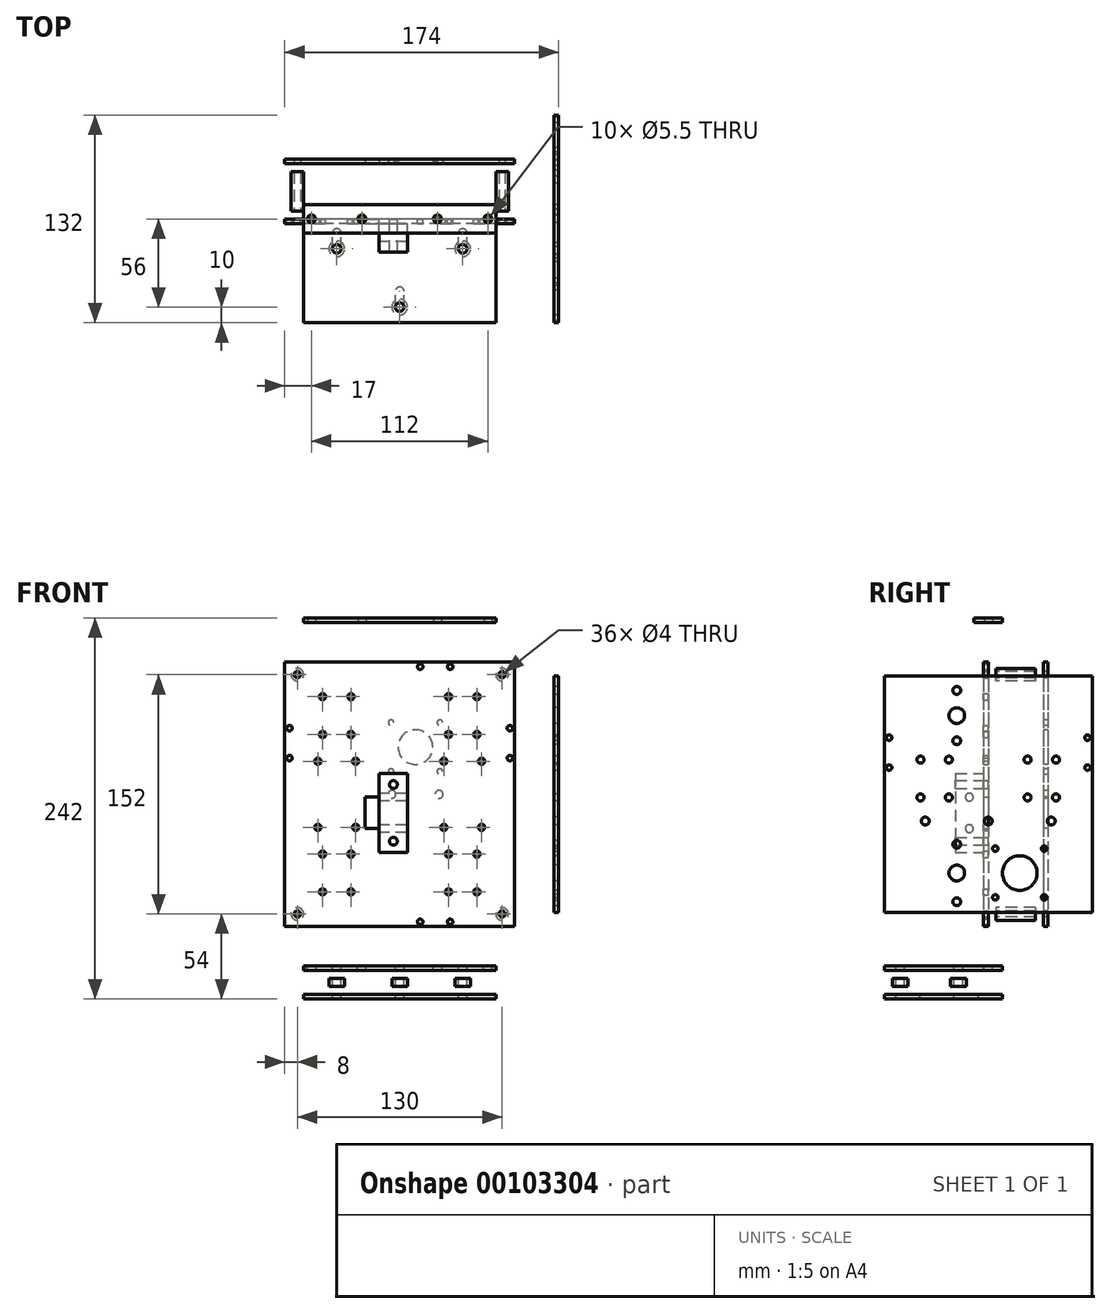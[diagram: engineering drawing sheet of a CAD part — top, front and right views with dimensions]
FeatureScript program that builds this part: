
annotation { "Feature Type Name" : "Feature", "Feature Type Description" : "" }
export const myFeature = defineFeature(function(context is Context, id is Id, definition is map)
    precondition{}
    {
        {
            assignVariable(context, id + "F0", {"name" : "Thickness", "anyValue" : 3});
        }
        {
            var Q0;
            Q0=qCreatedBy(makeId("Front.planeOp"),FACE);
            var sketch = newSketch(context, id + "F1", { "sketchPlane" : qUnion([Q0])});
            skLineSegment(sketch, "E0.bottom", {"start": v(73, 84) * mm, "end": v(-73, 84) * mm});
            skLineSegment(sketch, "E0.top", {"start": v(73, -84) * mm, "end": v(-73, -84) * mm});
            skLineSegment(sketch, "E0.left", {"start": v(73, 84) * mm, "end": v(73, -84) * mm});
            skLineSegment(sketch, "E0.right", {"start": v(-73, 84) * mm, "end": v(-73, -84) * mm});
            skPoint(sketch, "E0.middle", {"position": v(0, 0) * mm});
            skLineSegment(sketch, "E1", {"start": v(-49, -83.08) * mm, "end": v(-49, 79.73) * mm, "construction": true});
            skLineSegment(sketch, "E2", {"start": v(-31, -83.97) * mm, "end": v(-31, 79.73) * mm, "construction": true});
            skLineSegment(sketch, "E3", {"start": v(-55.64, 38) * mm, "end": v(56.55, 38) * mm, "construction": true});
            skLineSegment(sketch, "E4", {"start": v(-58.53, 62) * mm, "end": v(58.53, 62) * mm, "construction": true});
            skCircle(sketch, "E5", {"center": v(-49, 38) * mm, "radius": 2 * mm});
            skCircle(sketch, "E6", {"center": v(-49, 62) * mm, "radius": 2 * mm});
            skCircle(sketch, "E7", {"center": v(-31, 38) * mm, "radius": 2 * mm});
            skCircle(sketch, "E8", {"center": v(-31, 62) * mm, "radius": 2 * mm});
            skLineSegment(sketch, "E9", {"start": v(-72.74, 50) * mm, "end": v(58.97, 50) * mm, "construction": true});
            skLineSegment(sketch, "E10", {"start": v(-40, 79.29) * mm, "end": v(-40, -83.3) * mm, "construction": true});
            skLineSegment(sketch, "E11", {"start": v(-69.64, -50) * mm, "end": v(60.08, -50) * mm, "construction": true});
            skLineSegment(sketch, "E12", {"start": v(-58.61, -38) * mm, "end": v(58.75, -38) * mm, "construction": true});
            skLineSegment(sketch, "E13", {"start": v(-57.29, -62) * mm, "end": v(60.52, -62) * mm, "construction": true});
            skLineSegment(sketch, "E14", {"start": v(40, 79.29) * mm, "end": v(40, -84.85) * mm, "construction": true});
            skLineSegment(sketch, "E15", {"start": v(49, 79.07) * mm, "end": v(49, -84.4) * mm, "construction": true});
            skLineSegment(sketch, "E16", {"start": v(31, 79.29) * mm, "end": v(31, -83.74) * mm, "construction": true});
            skCircle(sketch, "E17", {"center": v(-49, -38) * mm, "radius": 2 * mm});
            skCircle(sketch, "E18", {"center": v(-31, -38) * mm, "radius": 2 * mm});
            skCircle(sketch, "E19", {"center": v(-49, -62) * mm, "radius": 2 * mm});
            skCircle(sketch, "E20", {"center": v(-31, -62) * mm, "radius": 2 * mm});
            skCircle(sketch, "E21", {"center": v(31, 62) * mm, "radius": 2 * mm});
            skCircle(sketch, "E22", {"center": v(49, 62) * mm, "radius": 2 * mm});
            skCircle(sketch, "E23", {"center": v(31, 38) * mm, "radius": 2 * mm});
            skCircle(sketch, "E24", {"center": v(49, 38) * mm, "radius": 2 * mm});
            skCircle(sketch, "E25", {"center": v(31, -38) * mm, "radius": 2 * mm});
            skCircle(sketch, "E26", {"center": v(49, -38) * mm, "radius": 2 * mm});
            skCircle(sketch, "E27", {"center": v(31, -62) * mm, "radius": 2 * mm});
            skCircle(sketch, "E28", {"center": v(49, -62) * mm, "radius": 2 * mm});
            skLineSegment(sketch, "E29", {"start": v(-70, 88.6) * mm, "end": v(-70, -88.82) * mm, "construction": true});
            skLineSegment(sketch, "E30", {"start": v(70, 90.06) * mm, "end": v(70, -91.23) * mm, "construction": true});
            skLineSegment(sketch, "E31", {"start": v(-72.75, 23) * mm, "end": v(68.8, 23) * mm, "construction": true});
            skCircle(sketch, "E32", {"center": v(-70, 23) * mm, "radius": 1.75 * mm});
            skCircle(sketch, "E33", {"center": v(70, 23) * mm, "radius": 1.75 * mm});
            skCircle(sketch, "E34", {"center": v(70, 42) * mm, "radius": 1.75 * mm});
            skCircle(sketch, "E35", {"center": v(-70, 42) * mm, "radius": 1.75 * mm});
            skLineSegment(sketch, "E36", {"start": v(-90.6, 21) * mm, "end": v(91.23, 21) * mm, "construction": true});
            skLineSegment(sketch, "E37", {"start": v(-89.18, -21) * mm, "end": v(89.82, -21) * mm, "construction": true});
            skLineSegment(sketch, "E38", {"start": v(28, 79.48) * mm, "end": v(28, -94.8) * mm, "construction": true});
            skLineSegment(sketch, "E39", {"start": v(52, 79.96) * mm, "end": v(52, -92.22) * mm, "construction": true});
            skLineSegment(sketch, "E40", {"start": v(-52, 80.9) * mm, "end": v(-52, -84.92) * mm, "construction": true});
            skLineSegment(sketch, "E41", {"start": v(-28, 79.72) * mm, "end": v(-28, -83.5) * mm, "construction": true});
            skCircle(sketch, "E42", {"center": v(-52, -21) * mm, "radius": 2 * mm});
            skCircle(sketch, "E43", {"center": v(-28, -21) * mm, "radius": 2 * mm});
            skCircle(sketch, "E44", {"center": v(-52, 21) * mm, "radius": 2 * mm});
            skCircle(sketch, "E45", {"center": v(-28, 21) * mm, "radius": 2 * mm});
            skCircle(sketch, "E46", {"center": v(28, 21) * mm, "radius": 2 * mm});
            skCircle(sketch, "E47", {"center": v(52, 21) * mm, "radius": 2 * mm});
            skCircle(sketch, "E48", {"center": v(52, -21) * mm, "radius": 2 * mm});
            skCircle(sketch, "E49", {"center": v(28, -21) * mm, "radius": 2 * mm});
            skLineSegment(sketch, "E50", {"start": v(-83.47, 81) * mm, "end": v(76.81, 81) * mm, "construction": true});
            skLineSegment(sketch, "E51", {"start": v(13, 80.28) * mm, "end": v(13, -83.41) * mm, "construction": true});
            skLineSegment(sketch, "E52", {"start": v(32, 79.81) * mm, "end": v(32, -83.41) * mm, "construction": true});
            skLineSegment(sketch, "E53", {"start": v(-76.56, -81) * mm, "end": v(71.61, -81) * mm, "construction": true});
            skCircle(sketch, "E54", {"center": v(13, -81) * mm, "radius": 1.75 * mm});
            skCircle(sketch, "E55", {"center": v(32, -81) * mm, "radius": 1.75 * mm});
            skCircle(sketch, "E56", {"center": v(13, 81) * mm, "radius": 1.75 * mm});
            skCircle(sketch, "E57", {"center": v(32, 81) * mm, "radius": 1.75 * mm});
            skCircle(sketch, "E58", {"center": v(-65, 76) * mm, "radius": 2 * mm});
            skCircle(sketch, "E59", {"center": v(65, 76) * mm, "radius": 2 * mm});
            skCircle(sketch, "E60", {"center": v(-65, -76) * mm, "radius": 2 * mm});
            skCircle(sketch, "E61", {"center": v(65, -76) * mm, "radius": 2 * mm});
            skLineSegment(sketch, "E62", {"start": v(-65, 88.6) * mm, "end": v(-65, -88.82) * mm, "construction": true});
            skLineSegment(sketch, "E63", {"start": v(65, 90.06) * mm, "end": v(65, -88.82) * mm, "construction": true});
            skLineSegment(sketch, "E64", {"start": v(-83.47, 76) * mm, "end": v(71.61, 76) * mm, "construction": true});
            skLineSegment(sketch, "E65", {"start": v(-76.56, -76) * mm, "end": v(71.61, -76) * mm, "construction": true});
            skLineSegment(sketch, "E66", {"start": v(-23, 79.72) * mm, "end": v(-23, -83.5) * mm, "construction": true});
            skLineSegment(sketch, "E67", {"start": v(-57, 81) * mm, "end": v(-57, -84.92) * mm, "construction": true});
            skLineSegment(sketch, "E68.bottom", {"start": v(-22, -1.8) * mm, "end": v(-13, -1.8) * mm});
            skLineSegment(sketch, "E68.top", {"start": v(-22, -21.8) * mm, "end": v(-13, -21.8) * mm});
            skLineSegment(sketch, "E68.left", {"start": v(-22, -1.8) * mm, "end": v(-22, -21.8) * mm});
            skLineSegment(sketch, "E68.right", {"start": v(-13, -1.8) * mm, "end": v(-13, -21.8) * mm});
            skLineSegment(sketch, "E69.bottom", {"start": v(-13, 13.2) * mm, "end": v(5, 13.2) * mm});
            skLineSegment(sketch, "E69.top", {"start": v(-13, -36.8) * mm, "end": v(5, -36.8) * mm});
            skLineSegment(sketch, "E69.left", {"start": v(-13, 13.2) * mm, "end": v(-13, -36.8) * mm});
            skLineSegment(sketch, "E69.right", {"start": v(5, 13.2) * mm, "end": v(5, -36.8) * mm});
            skLineSegment(sketch, "E70", {"start": v(-4, 17.89) * mm, "end": v(-4, -41.5) * mm, "construction": true});
            skCircle(sketch, "E71", {"center": v(-4, 6.2) * mm, "radius": 2.5 * mm});
            skCircle(sketch, "E72", {"center": v(-4, -29.8) * mm, "radius": 2.5 * mm});
            skLineSegment(sketch, "E73", {"start": v(-25.34, -11.8) * mm, "end": v(18.01, -11.8) * mm, "construction": true});
            skPoint(sketch, "E74", {"position": v(-4, 13.2) * mm});
            skPoint(sketch, "E75", {"position": v(-4, -11.8) * mm});
            skSolve(sketch);
        }
        {
            var Q0;
            Q0=makeQuery(id+"F1.imprint","IMPRINT",FACE,{"disambiguationData":[TD([[makeQuery(id+"F1.imprint","IMPRINT",EDGE,{"derivedFrom":sQuery(id+"F1.wireOp",EDGE,"E0.bottom")}),1.0]])]});
            var Q1;
            Q1=makeQuery(id+"F1.imprint","IMPRINT",FACE,{"disambiguationData":[TD([[makeQuery(id+"F1.imprint","IMPRINT",EDGE,{"derivedFrom":sQuery(id+"F1.wireOp",EDGE,"E69.bottom")}),-1.0]])]});
            extrude(context, id + "F2", {"entities" : qUnion([Q0, Q1]), "depth" : (getVariable(context, 'Thickness')) * mm});
        }
        {
            var Q0;
            Q0=makeQuery(id+"F1.imprint","IMPRINT",FACE,{"disambiguationData":[TD([[makeQuery(id+"F1.imprint","IMPRINT",EDGE,{"derivedFrom":sQuery(id+"F1.wireOp",EDGE,"E69.bottom")}),-1.0]])]});
            extrude(context, id + "F3", {"entities" : qUnion([Q0]), "depth" : 21 * mm, "hasSecondDirection" : true, "secondDirectionOppositeDirection" : false, "secondDirectionDepth" : 3 * mm});
        }
        {
            var Q0;
            Q0=makeQuery(id+"F3.opExtrude","SWEPT_FACE",FACE,{"disambiguationData":[OSD([sQuery(id+"F1.wireOp",EDGE,"E69.left")])]});
            var sketch = newSketch(context, id + "F4", { "sketchPlane" : qUnion([Q0])});
            skLineSegment(sketch, "E76", {"start": v(12, -1.15) * mm, "end": v(12, -40.85) * mm, "construction": true});
            skCircle(sketch, "E77", {"center": v(12, -1.8) * mm, "radius": 2.5 * mm});
            skCircle(sketch, "E78", {"center": v(12, -21.8) * mm, "radius": 2.5 * mm});
            skLineSegment(sketch, "E79", {"start": v(-1.92, -11.8) * mm, "end": v(22.84, -11.8) * mm, "construction": true});
            skCircle(sketch, "E80", {"center": v(12, -1.8) * mm, "radius": 9 * mm, "construction": true});
            skCircle(sketch, "E81", {"center": v(12, -21.8) * mm, "radius": 9 * mm, "construction": true});
            skSolve(sketch);
        }
        {
            var Q0;
            Q0=makeQuery(id+"F4.imprint","IMPRINT",FACE,{"disambiguationData":[TD([[makeQuery(id+"F4.imprint","IMPRINT",EDGE,{"derivedFrom":sQuery(id+"F4.wireOp",EDGE,"E77")}),1.0]])]});
            var Q1;
            Q1=makeQuery(id+"F4.imprint","IMPRINT",FACE,{"disambiguationData":[TD([[makeQuery(id+"F4.imprint","IMPRINT",EDGE,{"derivedFrom":sQuery(id+"F4.wireOp",EDGE,"E78")}),1.0]])]});
            extrude(context, id + "F5", {"entities" : qUnion([Q0, Q1]), "operationType" : NewBodyOperationType.REMOVE, "endBound" : BoundingType.THROUGH_ALL, "oppositeDirection" : true, "depth" : 25 * mm});
        }
        {
            var Q0;
            Q0=makeQuery(id+"F2.opExtrude","CAP_FACE",FACE,{"disambiguationData":[OSD([sQuery(id+"F1.wireOp",EDGE,"E0.bottom"),sQuery(id+"F1.wireOp",EDGE,"E0.top"),sQuery(id+"F1.wireOp",EDGE,"E0.left"),sQuery(id+"F1.wireOp",EDGE,"E0.right"),sQuery(id+"F1.wireOp",EDGE,"E5"),sQuery(id+"F1.wireOp",EDGE,"E6"),sQuery(id+"F1.wireOp",EDGE,"E7"),sQuery(id+"F1.wireOp",EDGE,"E8"),sQuery(id+"F1.wireOp",EDGE,"E17"),sQuery(id+"F1.wireOp",EDGE,"E18"),sQuery(id+"F1.wireOp",EDGE,"E19"),sQuery(id+"F1.wireOp",EDGE,"E20"),sQuery(id+"F1.wireOp",EDGE,"E21"),sQuery(id+"F1.wireOp",EDGE,"E22"),sQuery(id+"F1.wireOp",EDGE,"E23"),sQuery(id+"F1.wireOp",EDGE,"E24"),sQuery(id+"F1.wireOp",EDGE,"E25"),sQuery(id+"F1.wireOp",EDGE,"E26"),sQuery(id+"F1.wireOp",EDGE,"E27"),sQuery(id+"F1.wireOp",EDGE,"E28"),sQuery(id+"F1.wireOp",EDGE,"E32"),sQuery(id+"F1.wireOp",EDGE,"E33"),sQuery(id+"F1.wireOp",EDGE,"E34"),sQuery(id+"F1.wireOp",EDGE,"E35"),sQuery(id+"F1.wireOp",EDGE,"E42"),sQuery(id+"F1.wireOp",EDGE,"E43"),sQuery(id+"F1.wireOp",EDGE,"E44"),sQuery(id+"F1.wireOp",EDGE,"E45"),sQuery(id+"F1.wireOp",EDGE,"E46"),sQuery(id+"F1.wireOp",EDGE,"E47"),sQuery(id+"F1.wireOp",EDGE,"E48"),sQuery(id+"F1.wireOp",EDGE,"E49"),sQuery(id+"F1.wireOp",EDGE,"E54"),sQuery(id+"F1.wireOp",EDGE,"E55"),sQuery(id+"F1.wireOp",EDGE,"E56"),sQuery(id+"F1.wireOp",EDGE,"E57"),sQuery(id+"F1.wireOp",EDGE,"E58"),sQuery(id+"F1.wireOp",EDGE,"E59"),sQuery(id+"F1.wireOp",EDGE,"E60"),sQuery(id+"F1.wireOp",EDGE,"E61")])],"isStart":true});
            cPlane(context, id + "F6", {"entities" : qUnion([Q0]), "cplaneType" : CPlaneType.OFFSET, "offset" : 5 * mm, "width" : 150 * mm, "height" : 150 * mm});
        }
        {
            var Q0;
            Q0=qCreatedBy(id+"F6.planeOp",FACE);
            var sketch = newSketch(context, id + "F7", { "sketchPlane" : qUnion([Q0])});
            skCircle(sketch, "E82.0", {"center": v(65, 76) * mm, "radius": 2 * mm});
            skCircle(sketch, "E82.1", {"center": v(65, -76) * mm, "radius": 2 * mm});
            skCircle(sketch, "E82.2", {"center": v(-65, -76) * mm, "radius": 2 * mm});
            skCircle(sketch, "E82.3", {"center": v(-65, 76) * mm, "radius": 2 * mm});
            skCircle(sketch, "E83", {"center": v(65, 76) * mm, "radius": 4 * mm});
            skCircle(sketch, "E84", {"center": v(65, -76) * mm, "radius": 4 * mm});
            skCircle(sketch, "E85", {"center": v(-65, -76) * mm, "radius": 4 * mm});
            skCircle(sketch, "E86", {"center": v(-65, 76) * mm, "radius": 4 * mm});
            skSolve(sketch);
        }
        {
            var Q0;
            Q0=makeQuery(id+"F7.imprint","IMPRINT",FACE,{"disambiguationData":[TD([[makeQuery(id+"F7.imprint","IMPRINT",EDGE,{"derivedFrom":sQuery(id+"F7.wireOp",EDGE,"E82.0")}),-1.0]])]});
            var Q1;
            Q1=makeQuery(id+"F7.imprint","IMPRINT",FACE,{"disambiguationData":[TD([[makeQuery(id+"F7.imprint","IMPRINT",EDGE,{"derivedFrom":sQuery(id+"F7.wireOp",EDGE,"E82.1")}),-1.0]])]});
            var Q2;
            Q2=makeQuery(id+"F7.imprint","IMPRINT",FACE,{"disambiguationData":[TD([[makeQuery(id+"F7.imprint","IMPRINT",EDGE,{"derivedFrom":sQuery(id+"F7.wireOp",EDGE,"E82.2")}),-1.0]])]});
            var Q3;
            Q3=makeQuery(id+"F7.imprint","IMPRINT",FACE,{"disambiguationData":[TD([[makeQuery(id+"F7.imprint","IMPRINT",EDGE,{"derivedFrom":sQuery(id+"F7.wireOp",EDGE,"E82.3")}),-1.0]])]});
            extrude(context, id + "F8", {"entities" : qUnion([Q0, Q1, Q2, Q3]), "depth" : 25 * mm});
        }
        {
            var Q0;
            Q0=makeQuery(id+"F2.opExtrude","CAP_FACE",FACE,{"disambiguationData":[OSD([sQuery(id+"F1.wireOp",EDGE,"E0.bottom"),sQuery(id+"F1.wireOp",EDGE,"E0.top"),sQuery(id+"F1.wireOp",EDGE,"E0.left"),sQuery(id+"F1.wireOp",EDGE,"E0.right"),sQuery(id+"F1.wireOp",EDGE,"E5"),sQuery(id+"F1.wireOp",EDGE,"E6"),sQuery(id+"F1.wireOp",EDGE,"E7"),sQuery(id+"F1.wireOp",EDGE,"E8"),sQuery(id+"F1.wireOp",EDGE,"E17"),sQuery(id+"F1.wireOp",EDGE,"E18"),sQuery(id+"F1.wireOp",EDGE,"E19"),sQuery(id+"F1.wireOp",EDGE,"E20"),sQuery(id+"F1.wireOp",EDGE,"E21"),sQuery(id+"F1.wireOp",EDGE,"E22"),sQuery(id+"F1.wireOp",EDGE,"E23"),sQuery(id+"F1.wireOp",EDGE,"E24"),sQuery(id+"F1.wireOp",EDGE,"E25"),sQuery(id+"F1.wireOp",EDGE,"E26"),sQuery(id+"F1.wireOp",EDGE,"E27"),sQuery(id+"F1.wireOp",EDGE,"E28"),sQuery(id+"F1.wireOp",EDGE,"E32"),sQuery(id+"F1.wireOp",EDGE,"E33"),sQuery(id+"F1.wireOp",EDGE,"E34"),sQuery(id+"F1.wireOp",EDGE,"E35"),sQuery(id+"F1.wireOp",EDGE,"E42"),sQuery(id+"F1.wireOp",EDGE,"E43"),sQuery(id+"F1.wireOp",EDGE,"E44"),sQuery(id+"F1.wireOp",EDGE,"E45"),sQuery(id+"F1.wireOp",EDGE,"E46"),sQuery(id+"F1.wireOp",EDGE,"E47"),sQuery(id+"F1.wireOp",EDGE,"E48"),sQuery(id+"F1.wireOp",EDGE,"E49"),sQuery(id+"F1.wireOp",EDGE,"E54"),sQuery(id+"F1.wireOp",EDGE,"E55"),sQuery(id+"F1.wireOp",EDGE,"E56"),sQuery(id+"F1.wireOp",EDGE,"E57"),sQuery(id+"F1.wireOp",EDGE,"E58"),sQuery(id+"F1.wireOp",EDGE,"E59"),sQuery(id+"F1.wireOp",EDGE,"E60"),sQuery(id+"F1.wireOp",EDGE,"E61")])],"isStart":true});
            cPlane(context, id + "F9", {"entities" : qUnion([Q0]), "cplaneType" : CPlaneType.OFFSET, "offset" : 35 * mm, "width" : 150 * mm, "height" : 150 * mm});
        }
        {
            var Q0;
            Q0=qCreatedBy(id+"F9.planeOp",FACE);
            var sketch = newSketch(context, id + "F10", { "sketchPlane" : qUnion([Q0])});
            skLineSegment(sketch, "E87.0", {"start": v(-73, 84) * mm, "end": v(73, 84) * mm});
            skLineSegment(sketch, "E87.1", {"start": v(-73, 84) * mm, "end": v(-73, -84) * mm});
            skLineSegment(sketch, "E87.2", {"start": v(73, 84) * mm, "end": v(73, -84) * mm});
            skLineSegment(sketch, "E87.3", {"start": v(-73, -84) * mm, "end": v(73, -84) * mm});
            skLineSegment(sketch, "E87.4", {"start": v(22, -1.8) * mm, "end": v(22, -21.8) * mm});
            skLineSegment(sketch, "E87.5", {"start": v(13, -1.8) * mm, "end": v(13, -21.8) * mm});
            skLineSegment(sketch, "E87.6", {"start": v(22, -1.8) * mm, "end": v(13, -1.8) * mm});
            skLineSegment(sketch, "E87.7", {"start": v(22, -21.8) * mm, "end": v(13, -21.8) * mm});
            skLineSegment(sketch, "E88.bottom", {"start": v(-31, 51) * mm, "end": v(11, 51) * mm, "construction": true});
            skLineSegment(sketch, "E88.top", {"start": v(-31, 9) * mm, "end": v(11, 9) * mm, "construction": true});
            skLineSegment(sketch, "E88.left", {"start": v(-31, 51) * mm, "end": v(-31, 9) * mm, "construction": true});
            skLineSegment(sketch, "E88.right", {"start": v(11, 51) * mm, "end": v(11, 9) * mm, "construction": true});
            skLineSegment(sketch, "E89", {"start": v(-10, 94.34) * mm, "end": v(-10, -34.34) * mm, "construction": true});
            skLineSegment(sketch, "E90", {"start": v(-37.71, 30) * mm, "end": v(17.71, 30) * mm});
            skLineSegment(sketch, "E91.bottom", {"start": v(-25.5, 45.5) * mm, "end": v(5.5, 45.5) * mm, "construction": true});
            skLineSegment(sketch, "E91.top", {"start": v(-25.5, 14.5) * mm, "end": v(5.5, 14.5) * mm, "construction": true});
            skLineSegment(sketch, "E91.left", {"start": v(-25.5, 45.5) * mm, "end": v(-25.5, 14.5) * mm, "construction": true});
            skLineSegment(sketch, "E91.right", {"start": v(5.5, 45.5) * mm, "end": v(5.5, 14.5) * mm, "construction": true});
            skPoint(sketch, "E92", {"position": v(-10, 30) * mm});
            skCircle(sketch, "E93", {"center": v(-25.5, 45.5) * mm, "radius": 1.75 * mm});
            skCircle(sketch, "E94", {"center": v(5.5, 45.5) * mm, "radius": 1.75 * mm});
            skCircle(sketch, "E95", {"center": v(5.5, 14.5) * mm, "radius": 1.75 * mm});
            skCircle(sketch, "E96", {"center": v(-25.5, 14.5) * mm, "radius": 1.75 * mm});
            skCircle(sketch, "E97", {"center": v(-10, 30) * mm, "radius": 11 * mm});
            skLineSegment(sketch, "E98", {"start": v(-78.46, 0) * mm, "end": v(78.46, 0) * mm, "construction": true});
            skLineSegment(sketch, "E99", {"start": v(40, 94.7) * mm, "end": v(40, -94.7) * mm, "construction": true});
            skLineSegment(sketch, "E100", {"start": v(-40, 94.7) * mm, "end": v(-40, -94.7) * mm, "construction": true});
            skLineSegment(sketch, "E101", {"start": v(-79.3, -50) * mm, "end": v(80.19, -50) * mm, "construction": true});
            skLineSegment(sketch, "E102", {"start": v(80.19, 50) * mm, "end": v(-79.3, 50) * mm, "construction": true});
            skLineSegment(sketch, "E103", {"start": v(0, 94.7) * mm, "end": v(0, -94.7) * mm, "construction": true});
            skCircle(sketch, "E104.0", {"center": v(-65, 76) * mm, "radius": 2 * mm});
            skCircle(sketch, "E104.1", {"center": v(65, 76) * mm, "radius": 2 * mm});
            skCircle(sketch, "E104.2", {"center": v(65, -76) * mm, "radius": 2 * mm});
            skCircle(sketch, "E104.3", {"center": v(-65, -76) * mm, "radius": 2 * mm});
            skCircle(sketch, "E105", {"center": v(5, 0) * mm, "radius": 2.5 * mm});
            skCircle(sketch, "E106", {"center": v(-25, 0) * mm, "radius": 2.5 * mm});
            skCircle(sketch, "E107", {"center": v(-25, 0) * mm, "radius": 9 * mm, "construction": true});
            skCircle(sketch, "E108", {"center": v(5, 0) * mm, "radius": 9 * mm, "construction": true});
            skSolve(sketch);
        }
        {
            var Q0;
            Q0=makeQuery(id+"F10.imprint","IMPRINT",FACE,{"disambiguationData":[TD([[makeQuery(id+"F10.imprint","IMPRINT",EDGE,{"derivedFrom":sQuery(id+"F10.wireOp",EDGE,"E87.0")}),-1.0]])]});
            extrude(context, id + "F11", {"entities" : qUnion([Q0]), "depth" : (getVariable(context, 'Thickness')) * mm});
        }
        {
            var Q0;
            Q0=makeQuery(id+"F2.opExtrude","SWEPT_FACE",FACE,{"disambiguationData":[OSD([sQuery(id+"F1.wireOp",EDGE,"E0.bottom")])]});
            cPlane(context, id + "F12", {"entities" : qUnion([Q0]), "cplaneType" : CPlaneType.OFFSET, "offset" : 25 * mm, "width" : 150 * mm, "height" : 150 * mm});
        }
        {
            var Q0;
            Q0=qCreatedBy(id+"F12.planeOp",FACE);
            var sketch = newSketch(context, id + "F13", { "sketchPlane" : qUnion([Q0])});
            skLineSegment(sketch, "E109.bottom", {"start": v(61, -9) * mm, "end": v(-61, -9) * mm});
            skLineSegment(sketch, "E109.top", {"start": v(61, 9) * mm, "end": v(-61, 9) * mm});
            skLineSegment(sketch, "E109.left", {"start": v(61, -9) * mm, "end": v(61, 9) * mm});
            skLineSegment(sketch, "E109.right", {"start": v(-61, -9) * mm, "end": v(-61, 9) * mm});
            skPoint(sketch, "E109.middle", {"position": v(0, 0) * mm});
            skLineSegment(sketch, "E110", {"start": v(-40, -14.58) * mm, "end": v(-40, 18.52) * mm, "construction": true});
            skLineSegment(sketch, "E111", {"start": v(40, -14.81) * mm, "end": v(40, 21.3) * mm, "construction": true});
            skCircle(sketch, "E112", {"center": v(-56, 0) * mm, "radius": 2.5 * mm});
            skCircle(sketch, "E113", {"center": v(-24, 0) * mm, "radius": 2.5 * mm});
            skCircle(sketch, "E114", {"center": v(24, 0) * mm, "radius": 2.5 * mm});
            skCircle(sketch, "E115", {"center": v(56, 0) * mm, "radius": 2.5 * mm});
            skSolve(sketch);
        }
        {
            var Q0;
            Q0=makeQuery(id+"F13.imprint","IMPRINT",FACE,{"disambiguationData":[TD([[makeQuery(id+"F13.imprint","IMPRINT",EDGE,{"derivedFrom":sQuery(id+"F13.wireOp",EDGE,"E109.bottom")}),-1.0]])]});
            extrude(context, id + "F14", {"entities" : qUnion([Q0]), "depth" : (getVariable(context, 'Thickness')) * mm});
        }
        {
            var Q0;
            Q0=makeQuery(id+"F2.opExtrude","SWEPT_FACE",FACE,{"disambiguationData":[OSD([sQuery(id+"F1.wireOp",EDGE,"E0.top")])]});
            cPlane(context, id + "F15", {"entities" : qUnion([Q0]), "cplaneType" : CPlaneType.OFFSET, "offset" : 25 * mm, "width" : 150 * mm, "height" : 150 * mm});
        }
        {
            var Q0;
            Q0=qCreatedBy(id+"F15.planeOp",FACE);
            var sketch = newSketch(context, id + "F16", { "sketchPlane" : qUnion([Q0])});
            skLineSegment(sketch, "E116.bottom", {"start": v(61, -9) * mm, "end": v(-61, -9) * mm});
            skLineSegment(sketch, "E116.top", {"start": v(61, 66) * mm, "end": v(-61, 66) * mm});
            skLineSegment(sketch, "E116.left", {"start": v(61, -9) * mm, "end": v(61, 66) * mm});
            skLineSegment(sketch, "E116.right", {"start": v(-61, -9) * mm, "end": v(-61, 66) * mm});
            skPoint(sketch, "E116.middle", {"position": v(0, 28.5) * mm});
            skLineSegment(sketch, "E117", {"start": v(-62.7, 0) * mm, "end": v(63.63, 0) * mm, "construction": true});
            skCircle(sketch, "E118", {"center": v(-56, 0) * mm, "radius": 2.75 * mm});
            skCircle(sketch, "E119", {"center": v(-24, 0) * mm, "radius": 2.75 * mm});
            skCircle(sketch, "E120", {"center": v(24, 0) * mm, "radius": 2.75 * mm});
            skCircle(sketch, "E121", {"center": v(56, 0) * mm, "radius": 2.75 * mm});
            skLineSegment(sketch, "E122", {"start": v(60.53, 0) * mm, "end": v(-64.46, 0) * mm, "construction": true});
            skLineSegment(sketch, "E123", {"start": v(0, -36.2) * mm, "end": v(0, 36.61) * mm, "construction": true});
            skLineSegment(sketch, "E124", {"start": v(40, -36.2) * mm, "end": v(40, 36.61) * mm, "construction": true});
            skLineSegment(sketch, "E125", {"start": v(-40, -36.2) * mm, "end": v(-40, 36.61) * mm, "construction": true});
            skLineSegment(sketch, "E126", {"start": v(-62.32, 56) * mm, "end": v(63.27, 56) * mm, "construction": true});
            skLineSegment(sketch, "E127", {"start": v(-62.95, 19) * mm, "end": v(63.27, 19) * mm, "construction": true});
            skCircle(sketch, "E128", {"center": v(0, 56) * mm, "radius": 2.75 * mm});
            skCircle(sketch, "E129", {"center": v(-40, 19) * mm, "radius": 2.75 * mm});
            skCircle(sketch, "E130", {"center": v(40, 19) * mm, "radius": 2.75 * mm});
            skSolve(sketch);
        }
        {
            var Q0;
            Q0=makeQuery(id+"F16.imprint","IMPRINT",FACE,{"disambiguationData":[TD([[makeQuery(id+"F16.imprint","IMPRINT",EDGE,{"derivedFrom":sQuery(id+"F16.wireOp",EDGE,"E116.bottom")}),-1.0]])]});
            extrude(context, id + "F17", {"entities" : qUnion([Q0]), "depth" : (getVariable(context, 'Thickness')) * mm});
        }
        {
            var Q0;
            Q0=makeQuery(id+"F17.opExtrude","CAP_FACE",FACE,{"disambiguationData":[OSD([sQuery(id+"F16.wireOp",EDGE,"E116.bottom"),sQuery(id+"F16.wireOp",EDGE,"E116.top"),sQuery(id+"F16.wireOp",EDGE,"E116.left"),sQuery(id+"F16.wireOp",EDGE,"E116.right"),sQuery(id+"F16.wireOp",EDGE,"E118"),sQuery(id+"F16.wireOp",EDGE,"E119"),sQuery(id+"F16.wireOp",EDGE,"E120"),sQuery(id+"F16.wireOp",EDGE,"E121")])],"isStart":false});
            cPlane(context, id + "F18", {"entities" : qUnion([Q0]), "cplaneType" : CPlaneType.OFFSET, "offset" : 5 * mm, "width" : 150 * mm, "height" : 150 * mm});
        }
        {
            var Q0;
            Q0=qCreatedBy(id+"F18.planeOp",FACE);
            var sketch = newSketch(context, id + "F19", { "sketchPlane" : qUnion([Q0])});
            skCircle(sketch, "E131", {"center": v(0, 56) * mm, "radius": 5 * mm});
            skCircle(sketch, "E132", {"center": v(-40, 19) * mm, "radius": 5 * mm});
            skCircle(sketch, "E133", {"center": v(40, 19) * mm, "radius": 5 * mm});
            skCircle(sketch, "E134.0", {"center": v(-40, 19) * mm, "radius": 2.75 * mm});
            skCircle(sketch, "E135.0", {"center": v(0, 56) * mm, "radius": 2.75 * mm});
            skCircle(sketch, "E136.0", {"center": v(40, 19) * mm, "radius": 2.75 * mm});
            skSolve(sketch);
        }
        {
            var Q0;
            Q0=makeQuery(id+"F19.imprint","IMPRINT",FACE,{"disambiguationData":[TD([[makeQuery(id+"F19.imprint","IMPRINT",EDGE,{"derivedFrom":sQuery(id+"F19.wireOp",EDGE,"E132")}),1.0]])]});
            var Q1;
            Q1=makeQuery(id+"F19.imprint","IMPRINT",FACE,{"disambiguationData":[TD([[makeQuery(id+"F19.imprint","IMPRINT",EDGE,{"derivedFrom":sQuery(id+"F19.wireOp",EDGE,"E131")}),1.0]])]});
            var Q2;
            Q2=makeQuery(id+"F19.imprint","IMPRINT",FACE,{"disambiguationData":[TD([[makeQuery(id+"F19.imprint","IMPRINT",EDGE,{"derivedFrom":sQuery(id+"F19.wireOp",EDGE,"E133")}),1.0]])]});
            extrude(context, id + "F20", {"entities" : qUnion([Q0, Q1, Q2]), "depth" : 5 * mm});
        }
        {
            var Q0;
            Q0=makeQuery(id+"F17.opExtrude","CAP_FACE",FACE,{"disambiguationData":[OSD([sQuery(id+"F16.wireOp",EDGE,"E116.bottom"),sQuery(id+"F16.wireOp",EDGE,"E116.top"),sQuery(id+"F16.wireOp",EDGE,"E116.left"),sQuery(id+"F16.wireOp",EDGE,"E116.right"),sQuery(id+"F16.wireOp",EDGE,"E118"),sQuery(id+"F16.wireOp",EDGE,"E119"),sQuery(id+"F16.wireOp",EDGE,"E120"),sQuery(id+"F16.wireOp",EDGE,"E121"),sQuery(id+"F16.wireOp",EDGE,"E128"),sQuery(id+"F16.wireOp",EDGE,"E129"),sQuery(id+"F16.wireOp",EDGE,"E130")])],"isStart":false});
            cPlane(context, id + "F21", {"entities" : qUnion([Q0]), "cplaneType" : CPlaneType.OFFSET, "offset" : 15 * mm, "width" : 150 * mm, "height" : 150 * mm});
        }
        {
            var Q0;
            Q0=qCreatedBy(id+"F21.planeOp",FACE);
            var sketch = newSketch(context, id + "F22", { "sketchPlane" : qUnion([Q0])});
            skCircle(sketch, "E137.0", {"center": v(-40, 19) * mm, "radius": 2.75 * mm});
            skCircle(sketch, "E138.0", {"center": v(0, 56) * mm, "radius": 2.75 * mm});
            skCircle(sketch, "E139.0", {"center": v(40, 19) * mm, "radius": 2.75 * mm});
            skLineSegment(sketch, "E140.0", {"start": v(-61, -9) * mm, "end": v(-61, 66) * mm});
            skLineSegment(sketch, "E140.1", {"start": v(61, -9) * mm, "end": v(-61, -9) * mm});
            skLineSegment(sketch, "E140.2", {"start": v(61, -9) * mm, "end": v(61, 66) * mm});
            skLineSegment(sketch, "E140.3", {"start": v(61, 66) * mm, "end": v(-61, 66) * mm});
            skLineSegment(sketch, "E141", {"start": v(0, 56) * mm, "end": v(0, 46) * mm});
            skLineSegment(sketch, "E142", {"start": v(-40, 19) * mm, "end": v(-40, 9) * mm});
            skLineSegment(sketch, "E143", {"start": v(40, 19) * mm, "end": v(40, 9) * mm});
            skArc(sketch, "E144.0.startCap", {"start": v(-42.75, 19) * mm, "mid": v(-40, 21.75) * mm, "end": v(-37.25, 19) * mm});
            skArc(sketch, "E144.0.endCap", {"start": v(-37.25, 9) * mm, "mid": v(-40, 6.25) * mm, "end": v(-42.75, 9) * mm});
            skLineSegment(sketch, "E144.0.left", {"start": v(-37.25, 19) * mm, "end": v(-37.25, 9) * mm});
            skLineSegment(sketch, "E144.0.right", {"start": v(-42.75, 19) * mm, "end": v(-42.75, 9) * mm});
            skArc(sketch, "E144.1.startCap", {"start": v(-2.75, 56) * mm, "mid": v(0, 58.75) * mm, "end": v(2.75, 56) * mm});
            skArc(sketch, "E144.1.endCap", {"start": v(2.75, 46) * mm, "mid": v(0, 43.25) * mm, "end": v(-2.75, 46) * mm});
            skLineSegment(sketch, "E144.1.left", {"start": v(2.75, 56) * mm, "end": v(2.75, 46) * mm});
            skLineSegment(sketch, "E144.1.right", {"start": v(-2.75, 56) * mm, "end": v(-2.75, 46) * mm});
            skArc(sketch, "E144.2.startCap", {"start": v(37.25, 19) * mm, "mid": v(40, 21.75) * mm, "end": v(42.75, 19) * mm});
            skArc(sketch, "E144.2.endCap", {"start": v(42.75, 9) * mm, "mid": v(40, 6.25) * mm, "end": v(37.25, 9) * mm});
            skLineSegment(sketch, "E144.2.left", {"start": v(42.75, 19) * mm, "end": v(42.75, 9) * mm});
            skLineSegment(sketch, "E144.2.right", {"start": v(37.25, 19) * mm, "end": v(37.25, 9) * mm});
            skSolve(sketch);
        }
        {
            var Q0;
            Q0 = qSketchRegion(id + "F22", true);
            extrude(context, id + "F23", {"entities" : qUnion([Q0]), "depth" : (getVariable(context, 'Thickness')) * mm});
        }
        {
            var Q0;
            Q0=makeQuery(id+"F2.opExtrude","SWEPT_FACE",FACE,{"disambiguationData":[OSD([sQuery(id+"F1.wireOp",EDGE,"E0.left")])]});
            cPlane(context, id + "F24", {"entities" : qUnion([Q0]), "cplaneType" : CPlaneType.OFFSET, "offset" : 25 * mm, "width" : 150 * mm, "height" : 150 * mm});
        }
        {
            var Q0;
            Q0=qCreatedBy(id+"F24.planeOp",FACE);
            var sketch = newSketch(context, id + "F25", { "sketchPlane" : qUnion([Q0])});
            skLineSegment(sketch, "E145.bottom", {"start": v(-66, 75) * mm, "end": v(66, 75) * mm});
            skLineSegment(sketch, "E145.top", {"start": v(-66, -75) * mm, "end": v(66, -75) * mm});
            skLineSegment(sketch, "E145.left", {"start": v(-66, 75) * mm, "end": v(-66, -75) * mm});
            skLineSegment(sketch, "E145.right", {"start": v(66, 75) * mm, "end": v(66, -75) * mm});
            skPoint(sketch, "E146", {"position": v(0, 0) * mm});
            skLineSegment(sketch, "E147", {"start": v(-126.8, 0) * mm, "end": v(119.29, 0) * mm, "construction": true});
            skLineSegment(sketch, "E148", {"start": v(0, 95.8) * mm, "end": v(0, -127.28) * mm, "construction": true});
            skLineSegment(sketch, "E149", {"start": v(-20, 95.8) * mm, "end": v(-20, -127.28) * mm, "construction": true});
            skLineSegment(sketch, "E150", {"start": v(-126.8, 50) * mm, "end": v(119.29, 50) * mm, "construction": true});
            skLineSegment(sketch, "E151", {"start": v(-126.8, -50) * mm, "end": v(119.29, -50) * mm, "construction": true});
            skCircle(sketch, "E152", {"center": v(-20, 50) * mm, "radius": 5 * mm});
            skCircle(sketch, "E153", {"center": v(-20, -50) * mm, "radius": 5 * mm});
            skLineSegment(sketch, "E154", {"start": v(-40, 95.8) * mm, "end": v(-40, -127.28) * mm, "construction": true});
            skLineSegment(sketch, "E155", {"start": v(20, 95.8) * mm, "end": v(20, -127.28) * mm, "construction": true});
            skLineSegment(sketch, "E156", {"start": v(40, -127.28) * mm, "end": v(40, 95.8) * mm, "construction": true});
            skCircle(sketch, "E157", {"center": v(20, -50) * mm, "radius": 11 * mm});
            skLineSegment(sketch, "E158.bottom", {"start": v(41, -71) * mm, "end": v(-1, -71) * mm, "construction": true});
            skLineSegment(sketch, "E158.top", {"start": v(41, -29) * mm, "end": v(-1, -29) * mm, "construction": true});
            skLineSegment(sketch, "E158.left", {"start": v(41, -71) * mm, "end": v(41, -29) * mm, "construction": true});
            skLineSegment(sketch, "E158.right", {"start": v(-1, -71) * mm, "end": v(-1, -29) * mm, "construction": true});
            skLineSegment(sketch, "E159.bottom", {"start": v(35.5, -65.5) * mm, "end": v(4.5, -65.5) * mm, "construction": true});
            skLineSegment(sketch, "E159.top", {"start": v(35.5, -34.5) * mm, "end": v(4.5, -34.5) * mm, "construction": true});
            skLineSegment(sketch, "E159.left", {"start": v(35.5, -65.5) * mm, "end": v(35.5, -34.5) * mm, "construction": true});
            skLineSegment(sketch, "E159.right", {"start": v(4.5, -65.5) * mm, "end": v(4.5, -34.5) * mm, "construction": true});
            skCircle(sketch, "E160", {"center": v(4.5, -34.5) * mm, "radius": 1.75 * mm});
            skCircle(sketch, "E161", {"center": v(35.5, -34.5) * mm, "radius": 1.75 * mm});
            skCircle(sketch, "E162", {"center": v(4.5, -65.5) * mm, "radius": 1.75 * mm});
            skCircle(sketch, "E163", {"center": v(35.5, -65.5) * mm, "radius": 1.75 * mm});
            skCircle(sketch, "E164", {"center": v(-20, -31.75) * mm, "radius": 2.5 * mm});
            skCircle(sketch, "E165", {"center": v(-20, -68.25) * mm, "radius": 2.5 * mm});
            skLineSegment(sketch, "E166", {"start": v(-126.8, -17) * mm, "end": v(119.29, -17) * mm, "construction": true});
            skCircle(sketch, "E167", {"center": v(-40, -17) * mm, "radius": 2.5 * mm});
            skCircle(sketch, "E168", {"center": v(0, -17) * mm, "radius": 2.5 * mm});
            skCircle(sketch, "E169", {"center": v(40, -17) * mm, "radius": 2.5 * mm});
            skCircle(sketch, "E170", {"center": v(-20, 66) * mm, "radius": 2.5 * mm});
            skCircle(sketch, "E171", {"center": v(-20, 34) * mm, "radius": 2.5 * mm});
            skLineSegment(sketch, "E172", {"start": v(-63, 95.8) * mm, "end": v(-63, -127.28) * mm, "construction": true});
            skLineSegment(sketch, "E173", {"start": v(63, 95.8) * mm, "end": v(63, -127.28) * mm, "construction": true});
            skLineSegment(sketch, "E174", {"start": v(-126.8, 10) * mm, "end": v(119.29, 10) * mm, "construction": true});
            skLineSegment(sketch, "E175", {"start": v(-34, 95.8) * mm, "end": v(-34, -127.28) * mm, "construction": true});
            skLineSegment(sketch, "E176", {"start": v(34, 95.8) * mm, "end": v(34, -127.28) * mm, "construction": true});
            skLineSegment(sketch, "E177.bottom", {"start": v(-25, -2) * mm, "end": v(-43, -2) * mm, "construction": true});
            skLineSegment(sketch, "E177.top", {"start": v(-25, 22) * mm, "end": v(-43, 22) * mm, "construction": true});
            skLineSegment(sketch, "E177.left", {"start": v(-25, -2) * mm, "end": v(-25, 22) * mm, "construction": true});
            skLineSegment(sketch, "E177.right", {"start": v(-43, -2) * mm, "end": v(-43, 22) * mm, "construction": true});
            skPoint(sketch, "E177.middle", {"position": v(-34, 10) * mm});
            skLineSegment(sketch, "E178.bottom", {"start": v(43, -2) * mm, "end": v(25, -2) * mm, "construction": true});
            skLineSegment(sketch, "E178.top", {"start": v(43, 22) * mm, "end": v(25, 22) * mm, "construction": true});
            skLineSegment(sketch, "E178.left", {"start": v(43, -2) * mm, "end": v(43, 22) * mm, "construction": true});
            skLineSegment(sketch, "E178.right", {"start": v(25, -2) * mm, "end": v(25, 22) * mm, "construction": true});
            skPoint(sketch, "E178.middle", {"position": v(34, 10) * mm});
            skCircle(sketch, "E179", {"center": v(-43, 22) * mm, "radius": 2.25 * mm});
            skCircle(sketch, "E180", {"center": v(-25, 22) * mm, "radius": 2.25 * mm});
            skCircle(sketch, "E181", {"center": v(-25, -2) * mm, "radius": 2.25 * mm});
            skCircle(sketch, "E182", {"center": v(-43, -2) * mm, "radius": 2.25 * mm});
            skCircle(sketch, "E183", {"center": v(25, 22) * mm, "radius": 2.25 * mm});
            skCircle(sketch, "E184", {"center": v(43, 22) * mm, "radius": 2.25 * mm});
            skCircle(sketch, "E185", {"center": v(25, -2) * mm, "radius": 2.25 * mm});
            skCircle(sketch, "E186", {"center": v(43, -2) * mm, "radius": 2.25 * mm});
            skCircle(sketch, "E187", {"center": v(-63, 36) * mm, "radius": 1.75 * mm});
            skCircle(sketch, "E188", {"center": v(-63, 17) * mm, "radius": 1.75 * mm});
            skCircle(sketch, "E189", {"center": v(63, 36) * mm, "radius": 1.75 * mm});
            skCircle(sketch, "E190", {"center": v(63, 17) * mm, "radius": 1.75 * mm});
            skSolve(sketch);
        }
        {
            var Q0;
            Q0=makeQuery(id+"F25.imprint","IMPRINT",FACE,{"disambiguationData":[TD([[makeQuery(id+"F25.imprint","IMPRINT",EDGE,{"derivedFrom":sQuery(id+"F25.wireOp",EDGE,"E145.bottom")}),-1.0]])]});
            extrude(context, id + "F26", {"entities" : qUnion([Q0]), "depth" : (getVariable(context, 'Thickness')) * mm});
        }
    });
